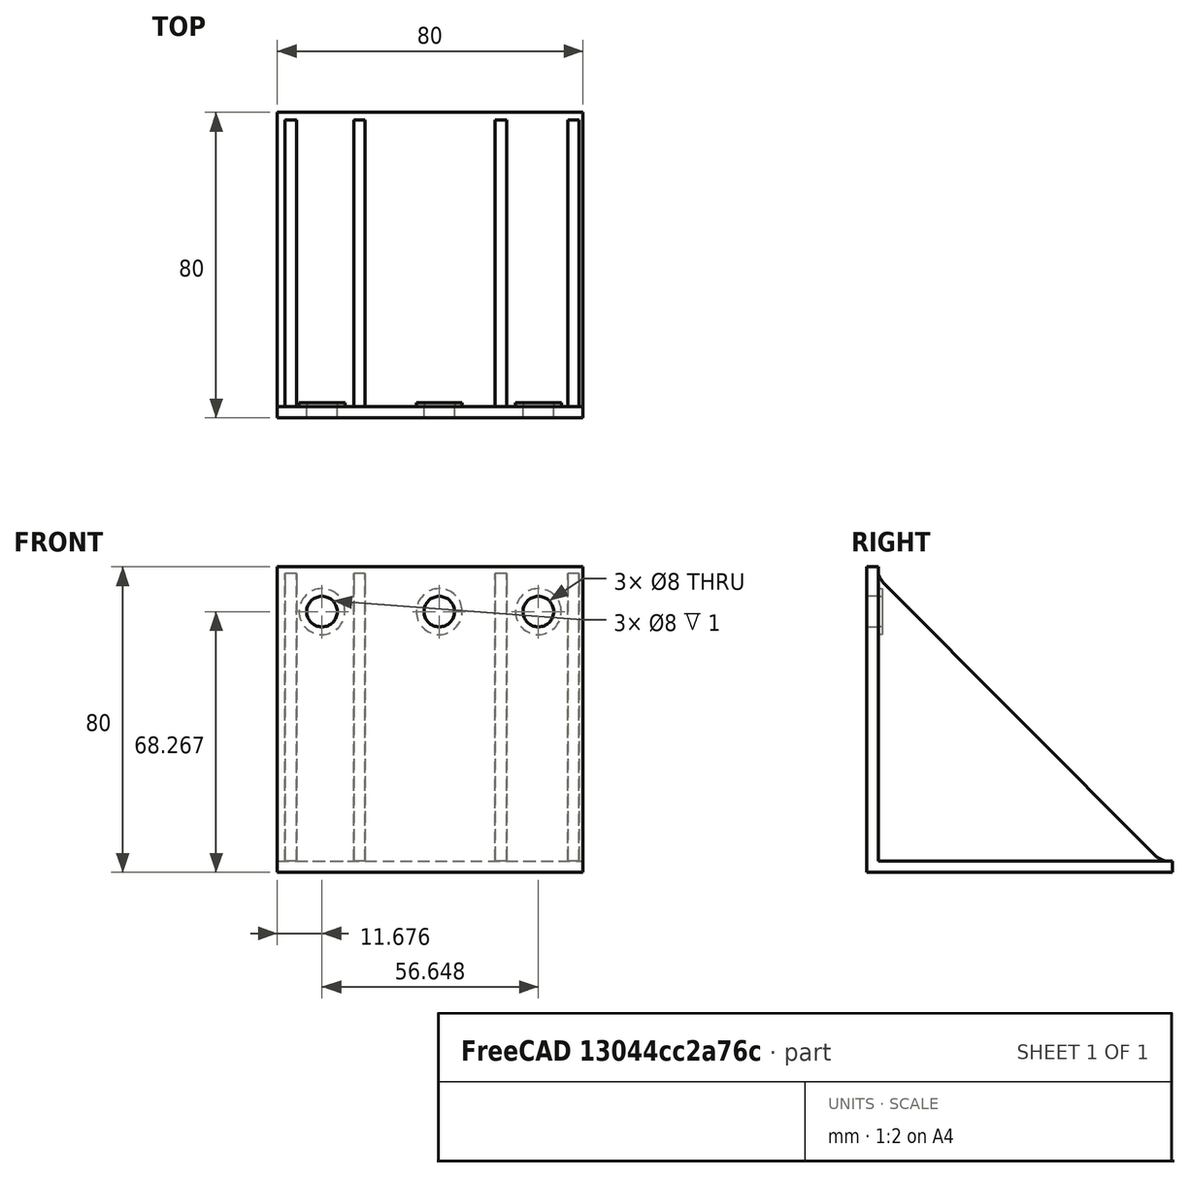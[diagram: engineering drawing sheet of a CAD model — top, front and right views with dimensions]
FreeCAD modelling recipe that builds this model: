
FCSTD DOCUMENT  (FreeCAD 0.18R16146 (Git))
Label: fem-konsole
License: All rights reserved
LicenseURL: http://en.wikipedia.org/wiki/All_rights_reserved
objects: PartDesign::Body×5, Sketcher::SketchObject×4, PartDesign::Pad×3, PartDesign::FeatureBase×3, Fem::FemSolverObjectPython×2, App::MaterialObjectPython×1, PartDesign::Pocket×1, Part::MultiFuse×1, Fem::FemMeshShapeNetgenObject×1, Fem::ConstraintFixed×1, Fem::ConstraintForce×1, Fem::FemAnalysis×1
note: 21 computed .brp shape members not serialized (recipe doc carries the construction recipe); baked Part::Feature solids carry a one-line shape summary decoded from their .brp

FEATURE [Sketcher::SketchObject] Sketch
  MapMode = 5
  Placement = pos=(0,0,0) rot=(0.57735,0.57735,0.57735;2.0944rad)
  Support = -> [YZ_Plane]
  sketch-geometry (6):
    g0: LineSegment StartX=0 StartY=0 StartZ=0 EndX=0 EndY=80 EndZ=0
    g1: LineSegment StartX=0 StartY=80 StartZ=0 EndX=3 EndY=80 EndZ=0
    g2: LineSegment StartX=3 StartY=80 StartZ=0 EndX=3 EndY=3 EndZ=0
    g3: LineSegment StartX=3 StartY=3 StartZ=0 EndX=80 EndY=3 EndZ=0
    g4: LineSegment StartX=80 StartY=3 StartZ=0 EndX=80 EndY=0 EndZ=0
    g5: LineSegment StartX=80 StartY=0 StartZ=0 EndX=0 EndY=0 EndZ=0
  constraints (17):
    c: Coincident(g-1,g0)
    c: Vertical(g0)
    c: Coincident(g0,g1)
    c: Horizontal(g1)
    c: Coincident(g1,g2)
    c: Vertical(g2)
    c: Coincident(g2,g3)
    c: Horizontal(g3)
    c: Coincident(g3,g4)
    c: Coincident(g4,g5)
    c: Coincident(g5,g0)
    c: Horizontal(g5)
    c: Equal(g1,g4)
    c: Equal(g2,g3)
    c: Vertical(g4)
    c: Distance(g0) = 80
    c: Distance(g1) = 3
FEATURE [PartDesign::Pad] Pad
  Length = 80
  Length2 = 100
  Placement = pos=(0,0,0) rot=(0.57735,0.57735,0.57735;2.0944rad)
  Profile = -> Sketch
  Type = 0
FEATURE [Sketcher::SketchObject] Sketch001
  MapMode = 5
  Placement = pos=(0,0,0) rot=(0.57735,0.57735,0.57735;2.0944rad)
  Support = -> [YZ_Plane001]
  sketch-geometry (9):
    g0: LineSegment StartX=79.8237 StartY=0 StartZ=0 EndX=0 EndY=0 EndZ=0
    g1: LineSegment StartX=0 StartY=0 StartZ=0 EndX=0 EndY=79.8237 EndZ=0
    g2: LineSegment StartX=0 StartY=79.8237 StartZ=0 EndX=2.832 EndY=79.8237 EndZ=0
    g3: LineSegment StartX=2.832 StartY=79.8237 StartZ=0 EndX=2.83193 EndY=79.5367 EndZ=0
    g4: LineSegment StartX=79.8237 StartY=0 StartZ=0 EndX=79.8237 EndY=2.83095 EndZ=0
    g5: LineSegment StartX=79.8237 StartY=2.83095 StartZ=0 EndX=79.4152 EndY=2.83095 EndZ=0
    g6: LineSegment StartX=4.39383 StartY=75.7551 StartZ=0 EndX=75.3964 EndY=4.4998 EndZ=0
    g7: ArcOfCircle CenterX=79.4152 CenterY=8.50439 CenterZ=0 NormalX=0 NormalY=0 NormalZ=1 AngleXU=0 Radius=5.67344 StartAngle=3.92521 EndAngle=4.71239
    g8: ArcOfCircle CenterX=8.18754 CenterY=79.5353 CenterZ=0 NormalX=0 NormalY=0 NormalZ=1 AngleXU=0 Radius=5.35561 StartAngle=3.14133 EndAngle=3.92521
  constraints (16):
    c: PointOnObject(g1,g-2)
    c: PointOnObject(g0,g-1)
    c: Coincident(g0,g-1)
    c: Coincident(g0,g1)
    c: Equal(g1,g0)
    c: Horizontal(g2)
    c: Coincident(g3,g2)
    c: Coincident(g4,g0)
    c: Vertical(g4)
    c: Coincident(g5,g4)
    c: Horizontal(g5)
    c: Tangent(g6,g7) = -1.5708
    c: Tangent(g5,g7) = 1.5708
    c: Tangent(g6,g8) = -1.5708
    c: Tangent(g3,g8) = -1.5708
    c: Coincident(g1,g2)
FEATURE [PartDesign::Pad] Pad001
  Length = 3
  Length2 = 100
  Placement = pos=(0,0,0) rot=(0.57735,0.57735,0.57735;2.0944rad)
  Profile = -> Sketch001
  Type = 0
FEATURE [PartDesign::Body] Body001
  Group = -> [Sketch001,Pad001]
  Origin = -> Origin001
  Placement = pos=(57,0,0) rot=(0,0,1;0rad)
  Tip = -> Pad001
FEATURE [PartDesign::FeatureBase] Clone
  BaseFeature = -> Body001
  Placement = pos=(61,0,0) rot=(0,0,1;0rad)
FEATURE [PartDesign::Body] Body002
  Group = -> [Clone]
  Origin = -> Origin002
  Placement = pos=(-41,0,0) rot=(0,0,1;0rad)
  Tip = -> Clone
FEATURE [Fem::FemSolverObjectPython] CalculiXccxTools  # FEM object (typed FeaturePython)
  AnalysisType = 0
  BeamShellResultOutput3D = false
  EigenmodeHighLimit = 1000000
  EigenmodeLowLimit = 0
  EigenmodesCount = 10
  GeometricalNonlinearity = 0
  IterationsControlParameterCutb = 0.25,0.5,0.75,0.85,,,1.5,
  IterationsControlParameterIter = 4,8,9,200,10,400,,200,,
  IterationsControlParameterTimeUse = false
  IterationsThermoMechMaximum = 200
  IterationsUserDefinedIncrementations = false
  IterationsUserDefinedTimeStepLength = false
  MaterialNonlinearity = 0
  MatrixSolverType = 0
  SplitInputWriter = false
  ThermoMechSteadyState = true
  TimeEnd = 1
  TimeInitialStep = 1
FEATURE [App::MaterialObjectPython] SolidMaterial  # material (typed FeaturePython)
  Category = 0
  Material = Density=1240 kg/m^3,+12 more (map truncated)
FEATURE [Fem::FemSolverObjectPython] CalculiXccxTools001  # FEM object (typed FeaturePython)
  AnalysisType = 0
  BeamShellResultOutput3D = false
  EigenmodeHighLimit = 1000000
  EigenmodeLowLimit = 0
  EigenmodesCount = 10
  GeometricalNonlinearity = 0
  IterationsControlParameterCutb = 0.25,0.5,0.75,0.85,,,1.5,
  IterationsControlParameterIter = 4,8,9,200,10,400,,200,,
  IterationsControlParameterTimeUse = false
  IterationsThermoMechMaximum = 200
  IterationsUserDefinedIncrementations = false
  IterationsUserDefinedTimeStepLength = false
  MaterialNonlinearity = 0
  MatrixSolverType = 0
  SplitInputWriter = false
  ThermoMechSteadyState = true
  TimeEnd = 1
  TimeInitialStep = 1
FEATURE [Sketcher::SketchObject] Sketch002
  ExternalGeometry = -> [Pad]
  MapMode = 5
  Placement = pos=(1.3e-15,3,-1e-15) rot=(0.57735,0.57735,0.57735;4.18879rad)
  Support = -> [Pad]
  sketch-geometry (5):
    g0: Circle CenterX=68.2673 CenterY=68.3241 CenterZ=0 NormalX=0 NormalY=0 NormalZ=1 AngleXU=0 Radius=4
    g1: Circle CenterX=68.2673 CenterY=11.6759 CenterZ=0 NormalX=0 NormalY=0 NormalZ=1 AngleXU=0 Radius=4
    g2: LineSegment [constr] StartX=68.2673 StartY=68.3241 StartZ=0 EndX=68.2673 EndY=80 EndZ=0
    g3: LineSegment [constr] StartX=68.2673 StartY=11.6759 StartZ=0 EndX=68.2673 EndY=-2.66e-14 EndZ=0
    g4: Circle CenterX=68.2673 CenterY=42.3777 CenterZ=0 NormalX=0 NormalY=0 NormalZ=1 AngleXU=0 Radius=4
  constraints (12):
    c: Equal(g0,g1)
    c: Vertical(g0,g1)
    c: Coincident(g2,g0)
    c: PointOnObject(g2,g-3)
    c: Coincident(g3,g1)
    c: PointOnObject(g3,g-4)
    c: Vertical(g3)
    c: Vertical(g2)
    c: Equal(g2,g3)
    c: Radius(g0) = 4
    c: Vertical(g4,g0)
    c: Equal(g4,g0)
FEATURE [PartDesign::Pocket] Pocket
  BaseFeature = -> Pad
  Length = 5
  Length2 = 100
  Placement = pos=(0,0,0) rot=(0.57735,0.57735,0.57735;2.0944rad)
  Profile = -> Sketch002
  Type = 1
FEATURE [PartDesign::FeatureBase] Clone001
  BaseFeature = -> Body001
  Placement = pos=(57,0,0) rot=(0,0,1;0rad)
FEATURE [PartDesign::Body] Body003
  Group = -> [Clone001]
  Origin = -> Origin003
  Placement = pos=(19,0,0) rot=(0,0,1;0rad)
  Tip = -> Clone001
FEATURE [PartDesign::FeatureBase] Clone002
  BaseFeature = -> Body001
  Placement = pos=(57,0,0) rot=(0,0,1;0rad)
FEATURE [PartDesign::Body] Body004
  Group = -> [Clone002]
  Origin = -> Origin004
  Placement = pos=(-55,0,0) rot=(0,0,1;0rad)
  Tip = -> Clone002
FEATURE [Sketcher::SketchObject] Sketch003
  ExternalGeometry = -> [Pocket]
  MapMode = 5
  Placement = pos=(1.3e-15,3,-2e-15) rot=(0.57735,0.57735,0.57735;4.18879rad)
  Support = -> [Pocket]
  sketch-geometry (6):
    g0: Circle CenterX=68.2673 CenterY=42.3777 CenterZ=0 NormalX=0 NormalY=0 NormalZ=1 AngleXU=0 Radius=4
    g1: Circle CenterX=68.2673 CenterY=42.3777 CenterZ=0 NormalX=0 NormalY=0 NormalZ=1 AngleXU=0 Radius=6
    g2: Circle CenterX=68.2673 CenterY=11.6759 CenterZ=0 NormalX=0 NormalY=0 NormalZ=1 AngleXU=0 Radius=4
    g3: Circle CenterX=68.2673 CenterY=11.6759 CenterZ=0 NormalX=0 NormalY=0 NormalZ=1 AngleXU=0 Radius=6
    g4: Circle CenterX=68.2673 CenterY=68.3241 CenterZ=0 NormalX=0 NormalY=0 NormalZ=1 AngleXU=0 Radius=4
    g5: Circle CenterX=68.2673 CenterY=68.3241 CenterZ=0 NormalX=0 NormalY=0 NormalZ=1 AngleXU=0 Radius=6
  constraints (12):
    c: Coincident(g0,g-4)
    c: Coincident(g1,g0)
    c: Coincident(g2,g-5)
    c: Coincident(g3,g2)
    c: Coincident(g4,g-3)
    c: Coincident(g5,g4)
    c: Equal(g4,g0)
    c: Equal(g0,g2)
    c: Radius(g4) = 4
    c: Equal(g5,g1)
    c: Equal(g1,g3)
    c: Radius(g5) = 6
FEATURE [PartDesign::Pad] Pad002
  BaseFeature = -> Pocket
  Length = 1
  Length2 = 100
  Placement = pos=(0,0,0) rot=(0.57735,0.57735,0.57735;2.0944rad)
  Profile = -> Sketch003
  Type = 0
FEATURE [PartDesign::Body] Body
  Group = -> [Sketch,Pad,Sketch002,Pocket,Sketch003,Pad002]
  Origin = -> Origin
  Tip = -> Pad002
FEATURE [Part::MultiFuse] Fusion
  Shapes = -> [Body,Body001,Body002,Body003,Body004]
FEATURE [Fem::FemMeshShapeNetgenObject] FEMMeshNetgen
  Fineness = 2
  GrowthRate = 0.3
  MaxSize = 1000
  NbSegsPerEdge = 1
  NbSegsPerRadius = 2
  Optimize = true
  SecondOrder = true
  Shape = -> Fusion
FEATURE [Fem::ConstraintFixed] FemConstraintFixed
  NormalDirection = (2e-16,-1.7e-15,-1)
  Normals = (16) [(1.66533e-16,-1.66533e-15,-1),(1.66533e-16,-1.66533e-15,-1),(1.66533e-16,-1.66533e-15,-1),(1.66533e-16,-1.66533e-15,-1),(1.66533e-16,-1.66533e-15,-1),+11 more]
  Points = (16) [(80,80,-1.19904e-13),(80,53.3333,-7.54952e-14),(80,26.6667,-3.10862e-14),(80,-1.81188e-13,1.33227e-14),(53.3333,80,-1.24345e-13),+11 more]
  References = -> [Fusion]
  Scale = 8
FEATURE [Fem::ConstraintForce] FemConstraintForce
  DirectionVector = (-6e-16,-1,7e-16)
  Force = 500
  NormalDirection = (6e-16,1,-7e-16)
  Points = (12) [(5.67592,4,68.2673),(11.6759,4,62.2673),(11.6759,4,74.2673),(17.6759,4,68.2673),(36.3777,4,68.2673),(42.3777,4,62.2673),(42.3777,4,74.2673),+5 more]
  References = -> [Pad002]
  Reversed = true
FEATURE [Fem::FemAnalysis] Analysis
  Group = -> [CalculiXccxTools,SolidMaterial,FEMMeshNetgen,CalculiXccxTools001,FemConstraintFixed,FemConstraintForce]
